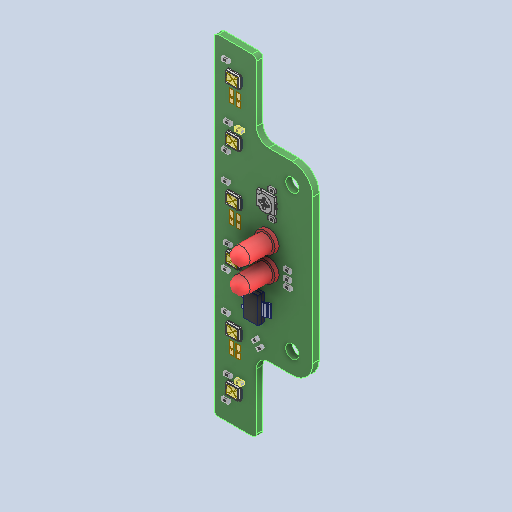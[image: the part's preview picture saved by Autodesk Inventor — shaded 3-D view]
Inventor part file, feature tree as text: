
AUTODESK INVENTOR PART (.ipt)
format: ipt  version: 2022 (Build 260153000, 153)  size: 4,764,672 bytes
history: native  units: mm
features: other x204, extrude x18
ambient origin geometry x8: Origin, YZ Plane, XZ Plane, XY Plane, X Axis, Y Axis, Z Axis, Center Point
bodies: Body1 (feature_tree), Body2 (feature_tree), Body3 (feature_tree), Body4 (feature_tree), Body5 (feature_tree), Body6 (feature_tree), Body7 (feature_tree), Body8 (feature_tree), Body9 (feature_tree), Body10 (feature_tree), Body11 (feature_tree), Body12 (feature_tree), Body13 (feature_tree), Body14 (feature_tree), Body15 (feature_tree), Body16 (feature_tree), Body17 (feature_tree), Body18 (feature_tree), Body19 (feature_tree), Body20 (feature_tree), Body21 (feature_tree), Body22 (feature_tree), Body23 (feature_tree), Body24 (feature_tree), Body25 (feature_tree), Body26 (feature_tree), Body27 (feature_tree), Body28 (feature_tree), Body29 (feature_tree), Body30 (feature_tree), Body31 (feature_tree), Body32 (feature_tree), Body33 (feature_tree), Body34 (feature_tree), Body35 (feature_tree), Body36 (feature_tree), Body37 (feature_tree), Body38 (feature_tree), Body39 (feature_tree), Body40 (feature_tree), Body41 (feature_tree), Body42 (feature_tree), Body43 (feature_tree), Body44 (feature_tree), Body45 (feature_tree), Body46 (feature_tree), Body47 (feature_tree), Body48 (feature_tree), Body49 (feature_tree), Body50 (feature_tree), Body51 (feature_tree), Body52 (feature_tree), Body53 (feature_tree), Body54 (feature_tree), Body55 (feature_tree), Body56 (feature_tree), Body57 (feature_tree), Body58 (feature_tree), Body59 (feature_tree), Body60 (feature_tree), Body61 (feature_tree), Body62 (feature_tree), Body63 (feature_tree), Body64 (feature_tree), Body65 (feature_tree), Body66 (feature_tree), Body67 (feature_tree), Body68 (feature_tree), Body69 (feature_tree), Body70 (feature_tree), Body71 (feature_tree), Body72 (feature_tree), Body73 (feature_tree), Body74 (feature_tree), Body75 (feature_tree), Body76 (feature_tree), Body77 (feature_tree), Body78 (feature_tree), Body79 (feature_tree), Body80 (feature_tree), Body81 (feature_tree), Body82 (feature_tree), Body83 (feature_tree), Body84 (feature_tree), Body85 (feature_tree), Body86 (feature_tree), Body87 (feature_tree), Body88 (feature_tree), Body89 (feature_tree), Body90 (feature_tree), Body91 (feature_tree), Body92 (feature_tree), Body93 (feature_tree), Body94 (feature_tree), Body95 (feature_tree), Body96 (feature_tree), Body97 (feature_tree), Body98 (feature_tree), Body99 (feature_tree), Body100 (feature_tree), Body101 (feature_tree), Body102 (feature_tree), Body103 (feature_tree), Body104 (feature_tree), Body105 (feature_tree), Body106 (feature_tree), Body107 (feature_tree), Body108 (feature_tree), Body109 (feature_tree), Body110 (feature_tree), Body111 (feature_tree)
feature tree (222):
  other  "Твердое тело1"
  other  "Твердое тело2"
  other  "Твердое тело3"
  other  "Твердое тело4"
  other  "Твердое тело5"
  other  "Твердое тело6"
  other  "Твердое тело7"
  other  "Твердое тело8"
  other  "Твердое тело9"
  other  "Твердое тело10"
  other  "Твердое тело11"
  other  "Твердое тело12"
  other  "Твердое тело13"
  other  "Твердое тело14"
  other  "Твердое тело15"
  other  "Твердое тело16"
  other  "Твердое тело17"
  other  "Твердое тело18"
  other  "Твердое тело19"
  other  "Твердое тело20"
  other  "Твердое тело21"
  other  "Твердое тело22"
  other  "Твердое тело23"
  other  "Твердое тело24"
  other  "Твердое тело25"
  other  "Твердое тело26"
  other  "Твердое тело27"
  other  "Твердое тело28"
  other  "Твердое тело29"
  other  "Твердое тело30"
  other  "Твердое тело31"
  other  "Твердое тело32"
  other  "Твердое тело33"
  other  "Твердое тело34"
  other  "Твердое тело35"
  other  "Твердое тело36"
  other  "Твердое тело37"
  other  "Твердое тело38"
  other  "Твердое тело39"
  other  "Твердое тело40"
  other  "Твердое тело41"
  other  "Твердое тело42"
  other  "Твердое тело43"
  other  "Твердое тело44"
  other  "Твердое тело45"
  other  "Твердое тело46"
  other  "Твердое тело47"
  other  "Твердое тело48"
  other  "Твердое тело49"
  other  "Твердое тело50"
  other  "Твердое тело51"
  other  "Твердое тело52"
  other  "Твердое тело53"
  other  "Твердое тело54"
  other  "Твердое тело55"
  other  "Твердое тело56"
  other  "Твердое тело57"
  other  "Твердое тело58"
  other  "Твердое тело59"
  other  "Твердое тело60"
  other  "Твердое тело61"
  other  "Твердое тело62"
  other  "Твердое тело63"
  other  "Твердое тело64"
  other  "Твердое тело65"
  other  "Твердое тело66"
  other  "Твердое тело67"
  other  "Твердое тело68"
  other  "Твердое тело69"
  other  "Твердое тело70"
  other  "Твердое тело71"
  other  "Твердое тело72"
  other  "Твердое тело73"
  other  "Твердое тело74"
  other  "Твердое тело75"
  other  "Твердое тело76"
  other  "Твердое тело77"
  other  "Твердое тело78"
  other  "Твердое тело79"
  other  "Твердое тело80"
  other  "Твердое тело81"
  other  "Твердое тело82"
  other  "Твердое тело83"
  other  "Твердое тело84"
  other  "Твердое тело85"
  other  "Твердое тело86"
  other  "Твердое тело87"
  other  "Твердое тело88"
  other  "Твердое тело89"
  other  "Твердое тело90"
  other  "Твердое тело91"
  other  "Твердое тело92"
  other  "Твердое тело93"
  other  "Твердое тело94"
  other  "Твердое тело95"
  other  "Твердое тело96"
  other  "Твердое тело97"
  other  "Твердое тело98"
  other  "Твердое тело99"
  other  "Твердое тело100"
  other  "Твердое тело101"
  other  "Твердое тело102"
  other  "Твердое тело103"
  other  "Твердое тело104"
  other  "Твердое тело105"
  other  "Твердое тело106"
  other  "Твердое тело107"
  other  "Твердое тело108"
  other  "Твердое тело109"
  other  "Твердое тело110"
  other  "Твердое тело111"
  other  "Open CASCADE STEP translator 7.5 4.1.1_1561:1"
  other  "CircuitWorks-SOT-223_1563:1"
  extrude  "Extruded_1565:1"  [1 undecoded]
  extrude  "Extruded_1567:1"  [1 undecoded]
  extrude  "Extruded_1565:2"  [1 undecoded]
  extrude  "Extruded_1567:2"  [1 undecoded]
  extrude  "Extruded_1565:3"  [1 undecoded]
  extrude  "Extruded_1567:3"  [1 undecoded]
  extrude  "Extruded_1565:4"  [1 undecoded]
  extrude  "Extruded_1567:4"  [1 undecoded]
  extrude  "Extruded_1565:5"  [1 undecoded]
  extrude  "Extruded_1567:5"  [1 undecoded]
  extrude  "Extruded_1565:6"  [1 undecoded]
  extrude  "Extruded_1567:6"  [1 undecoded]
  extrude  "Extruded_1585:1"  [1 undecoded]
  extrude  "Extruded_1585:2"  [1 undecoded]
  extrude  "Extruded_1588:1"  [1 undecoded]
  extrude  "Extruded_1585:3"  [1 undecoded]
  extrude  "Extruded_1585:4"  [1 undecoded]
  extrude  "Extruded_1588:2"  [1 undecoded]
  other  "RESC1608_1595:1"
  other  "RESC1608_1597:1"
  other  "RESC1608_1599:1"
  other  "RESC1608_1601:1"
  other  "RESC1608_1603:1"
  other  "RESC1608_1605:1"
  other  "RESC1608_1607:1"
  other  "RESC1608_1609:1"
  other  "CAPC0603_1611:1"
  other  "CAPC0603_1613:1"
  other  "CAPC0603_1615:1"
  other  "Open CASCADE STEP translator 7.5 4.22.1.1_1617:1"
  other  "Open CASCADE STEP translator 7.5 4.22.1.2_1618:1"
  other  "Open CASCADE STEP translator 7.5 4.22.1.3_1619:1"
  other  "Open CASCADE STEP translator 7.5 4.22.1.4_1620:1"
  other  "Open CASCADE STEP translator 7.5 4.22.1.5_1621:1"
  other  "Open CASCADE STEP translator 7.5 4.22.1.6_1622:1"
  other  "Open CASCADE STEP translator 7.5 4.22.1.7_1623:1"
  other  "Open CASCADE STEP translator 7.5 4.22.1.8_1624:1"
  other  "Open CASCADE STEP translator 7.5 4.22.1.9_1625:1"
  other  "Open CASCADE STEP translator 7.5 4.22.1.10_1626:1"
  other  "Open CASCADE STEP translator 7.5 4.22.1.11_1627:1"
  other  "Open CASCADE STEP translator 7.5 4.22.1.12_1628:1"
  other  "Open CASCADE STEP translator 7.5 4.22.1.13_1629:1"
  other  "Open CASCADE STEP translator 7.5 4.22.1.14_1630:1"
  other  "Open CASCADE STEP translator 7.5 4.22.1.15_1631:1"
  other  "Open CASCADE STEP translator 7.5 4.22.1.16_1632:1"
  other  "Open CASCADE STEP translator 7.5 4.22.1.17_1633:1"
  other  "Open CASCADE STEP translator 7.5 4.22.1.18_1634:1"
  other  "Open CASCADE STEP translator 7.5 4.22.1.19_1635:1"
  other  "Open CASCADE STEP translator 7.5 4.22.1.20_1636:1"
  other  "Open CASCADE STEP translator 7.5 4.22.1.21_1637:1"
  other  "Open CASCADE STEP translator 7.5 4.22.1.22_1638:1"
  other  "Open CASCADE STEP translator 7.5 4.22.1.23_1639:1"
  other  "Open CASCADE STEP translator 7.5 4.22.1.24_1640:1"
  other  "Open CASCADE STEP translator 7.5 4.22.1.25_1641:1"
  other  "Open CASCADE STEP translator 7.5 4.22.1.26_1642:1"
  other  "Open CASCADE STEP translator 7.5 4.22.1.27_1643:1"
  other  "Open CASCADE STEP translator 7.5 4.22.1.28_1644:1"
  other  "Open CASCADE STEP translator 7.5 4.22.1.29_1645:1"
  other  "Open CASCADE STEP translator 7.5 4.22.1.30_1646:1"
  other  "Open CASCADE STEP translator 7.5 4.22.1.31_1647:1"
  other  "Open CASCADE STEP translator 7.5 4.22.1.32_1648:1"
  other  "Open CASCADE STEP translator 7.5 4.22.1.33_1649:1"
  other  "Open CASCADE STEP translator 7.5 4.22.1.34_1650:1"
  other  "Open CASCADE STEP translator 7.5 4.22.1.35_1651:1"
  other  "Open CASCADE STEP translator 7.5 4.22.1.36_1652:1"
  other  "Open CASCADE STEP translator 7.5 4.22.1.37_1653:1"
  other  "Open CASCADE STEP translator 7.5 4.22.1.38_1654:1"
  other  "Open CASCADE STEP translator 7.5 4.22.1.39_1655:1"
  other  "Open CASCADE STEP translator 7.5 4.22.1.40_1656:1"
  other  "Open CASCADE STEP translator 7.5 4.22.1.41_1657:1"
  other  "Open CASCADE STEP translator 7.5 4.22.1.42_1658:1"
  other  "Open CASCADE STEP translator 7.5 4.22.1.43_1659:1"
  other  "Open CASCADE STEP translator 7.5 4.22.1.44_1660:1"
  other  "Open CASCADE STEP translator 7.5 4.22.1.45_1661:1"
  other  "Open CASCADE STEP translator 7.5 4.22.1.46_1662:1"
  other  "SW3DPS-5MM LED RED-DEFAULT_1665:1"
  other  "User Library-LED_2835_Samsung_SPMWH1228_1667:1"
  other  "User Library-LED_2835_Samsung_SPMWH1228_1667:2"
  other  "User Library-LED_2835_Samsung_SPMWH1228_1667:3"
  other  "User Library-LED_2835_Samsung_SPMWH1228_1667:4"
  other  "User Library-LED_2835_Samsung_SPMWH1228_1669:1"
  other  "User Library-LED_2835_Samsung_SPMWH1228_1669:2"
  other  "User Library-LED_2835_Samsung_SPMWH1228_1669:3"
  other  "User Library-LED_2835_Samsung_SPMWH1228_1669:4"
  other  "User Library-LED_2835_Samsung_SPMWH1228_1671:1"
  other  "User Library-LED_2835_Samsung_SPMWH1228_1671:2"
  other  "User Library-LED_2835_Samsung_SPMWH1228_1671:3"
  other  "User Library-LED_2835_Samsung_SPMWH1228_1671:4"
  other  "User Library-LED_2835_Samsung_SPMWH1228_1673:1"
  other  "User Library-LED_2835_Samsung_SPMWH1228_1673:2"
  other  "User Library-LED_2835_Samsung_SPMWH1228_1673:3"
  other  "User Library-LED_2835_Samsung_SPMWH1228_1673:4"
  other  "User Library-LED_2835_Samsung_SPMWH1228_1675:1"
  other  "User Library-LED_2835_Samsung_SPMWH1228_1675:2"
  other  "User Library-LED_2835_Samsung_SPMWH1228_1675:3"
  other  "User Library-LED_2835_Samsung_SPMWH1228_1675:4"
  other  "User Library-LED_2835_Samsung_SPMWH1228_1677:1"
  other  "User Library-LED_2835_Samsung_SPMWH1228_1677:2"
  other  "User Library-LED_2835_Samsung_SPMWH1228_1677:3"
  other  "User Library-LED_2835_Samsung_SPMWH1228_1677:4"
  other  "RESC1608_1679:1"
  other  "RESC1608_1681:1"
  other  "Open CASCADE STEP translator 7.5 4.32.1.1_1683:1"
  other  "Open CASCADE STEP translator 7.5 4.32.1.2_1684:1"
  other  "RESC1608_1687:1"
  other  "RESC1608_1689:1"
  other  "RESC1608_1691:1"
  other  "RESC1608_1693:1"
  other  "SW3DPS-5MM LED RED-DEFAULT_1695:1"
note: 18 required parameter values undecoded (feature->parameter linkage not recoverable at this tier; creation-order binding heuristic only, values carry confidence <= 0.55)
